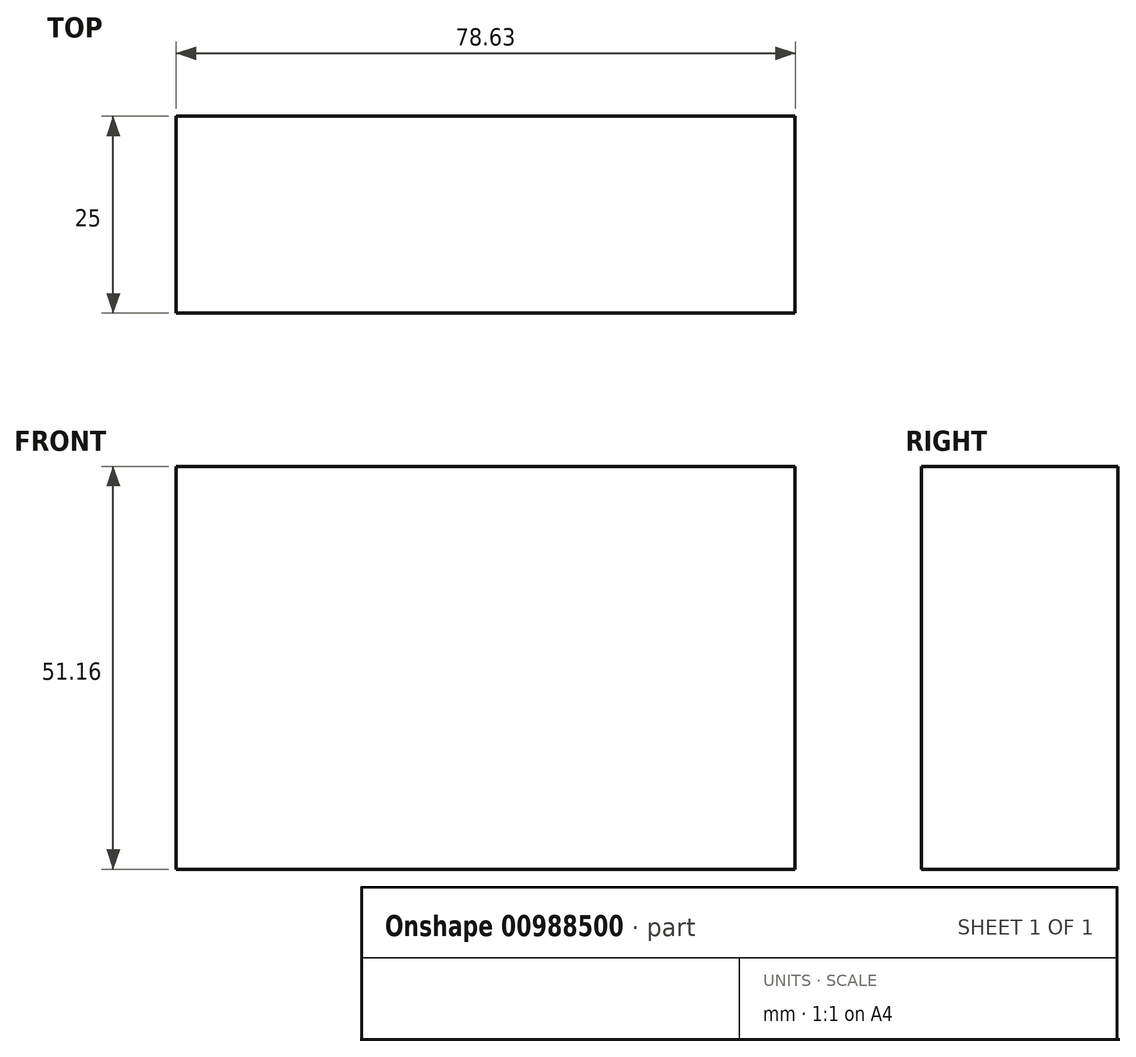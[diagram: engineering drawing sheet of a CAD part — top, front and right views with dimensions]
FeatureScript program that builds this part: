
annotation { "Feature Type Name" : "Feature", "Feature Type Description" : "" }
export const myFeature = defineFeature(function(context is Context, id is Id, definition is map)
    precondition{}
    {
        {
            var Q0;
            Q0=qCreatedBy(makeId("Front.planeOp"),FACE);
            var sketch = newSketch(context, id + "F0", { "sketchPlane" : qUnion([Q0])});
            skLineSegment(sketch, "E0.bottom", {"start": v(-94.67, 28.18) * mm, "end": v(-16.04, 28.18) * mm});
            skLineSegment(sketch, "E0.top", {"start": v(-94.67, -22.98) * mm, "end": v(-16.04, -22.98) * mm});
            skLineSegment(sketch, "E0.left", {"start": v(-94.67, 28.18) * mm, "end": v(-94.67, -22.98) * mm});
            skLineSegment(sketch, "E0.right", {"start": v(-16.04, 28.18) * mm, "end": v(-16.04, -22.98) * mm});
            skSolve(sketch);
        }
        {
            var Q0;
            Q0=makeQuery(id+"F0.imprint","IMPRINT",FACE,{"disambiguationData":[TD([[makeQuery(id+"F0.imprint","IMPRINT",EDGE,{"derivedFrom":sQuery(id+"F0.wireOp",EDGE,"E0.bottom")}),-1.0]])]});
            extrude(context, id + "F1", {"entities" : qUnion([Q0]), "depth" : 25 * mm, "offsetDistance" : 25 * mm});
        }
    });
